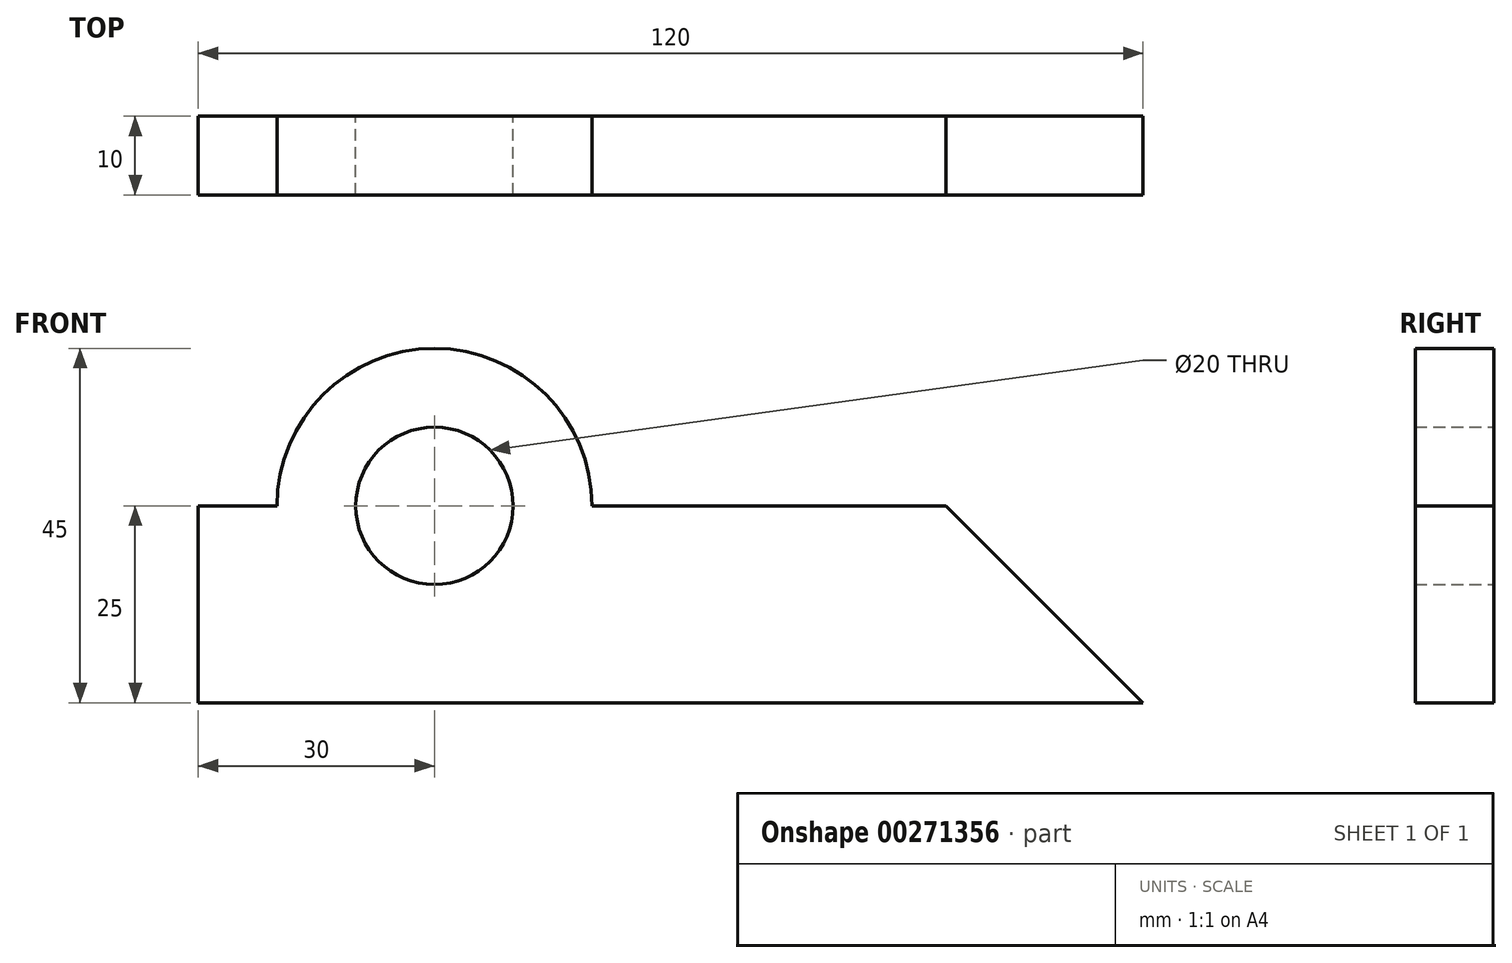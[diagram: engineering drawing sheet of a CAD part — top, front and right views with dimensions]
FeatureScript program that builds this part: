
annotation { "Feature Type Name" : "Feature", "Feature Type Description" : "" }
export const myFeature = defineFeature(function(context is Context, id is Id, definition is map)
    precondition{}
    {
        {
            var Q0;
            Q0=qCreatedBy(makeId("Front.planeOp"),FACE);
            var sketch = newSketch(context, id + "F0", { "sketchPlane" : qUnion([Q0])});
            skLineSegment(sketch, "E0", {"start": v(0, 0) * mm, "end": v(120, 0) * mm});
            skLineSegment(sketch, "E1", {"start": v(120, 0) * mm, "end": v(95, 25) * mm});
            skLineSegment(sketch, "E2", {"start": v(0, 0) * mm, "end": v(0, 25) * mm});
            skArc(sketch, "E3", {"start": v(50, 25) * mm, "mid": v(30, 45) * mm, "end": v(10, 25) * mm});
            skLineSegment(sketch, "E4", {"start": v(50, 25) * mm, "end": v(95, 25) * mm});
            skLineSegment(sketch, "E5", {"start": v(10, 25) * mm, "end": v(0, 25) * mm});
            skCircle(sketch, "E6", {"center": v(30, 25) * mm, "radius": 10 * mm});
            skSolve(sketch);
        }
        {
            var Q0;
            Q0=makeQuery(id+"F0.imprint","IMPRINT",FACE,{"disambiguationData":[TD([[makeQuery(id+"F0.imprint","IMPRINT",EDGE,{"derivedFrom":sQuery(id+"F0.wireOp",EDGE,"E0")}),1.0]])]});
            extrude(context, id + "F1", {"entities" : qUnion([Q0]), "depth" : 10 * mm});
        }
    });
